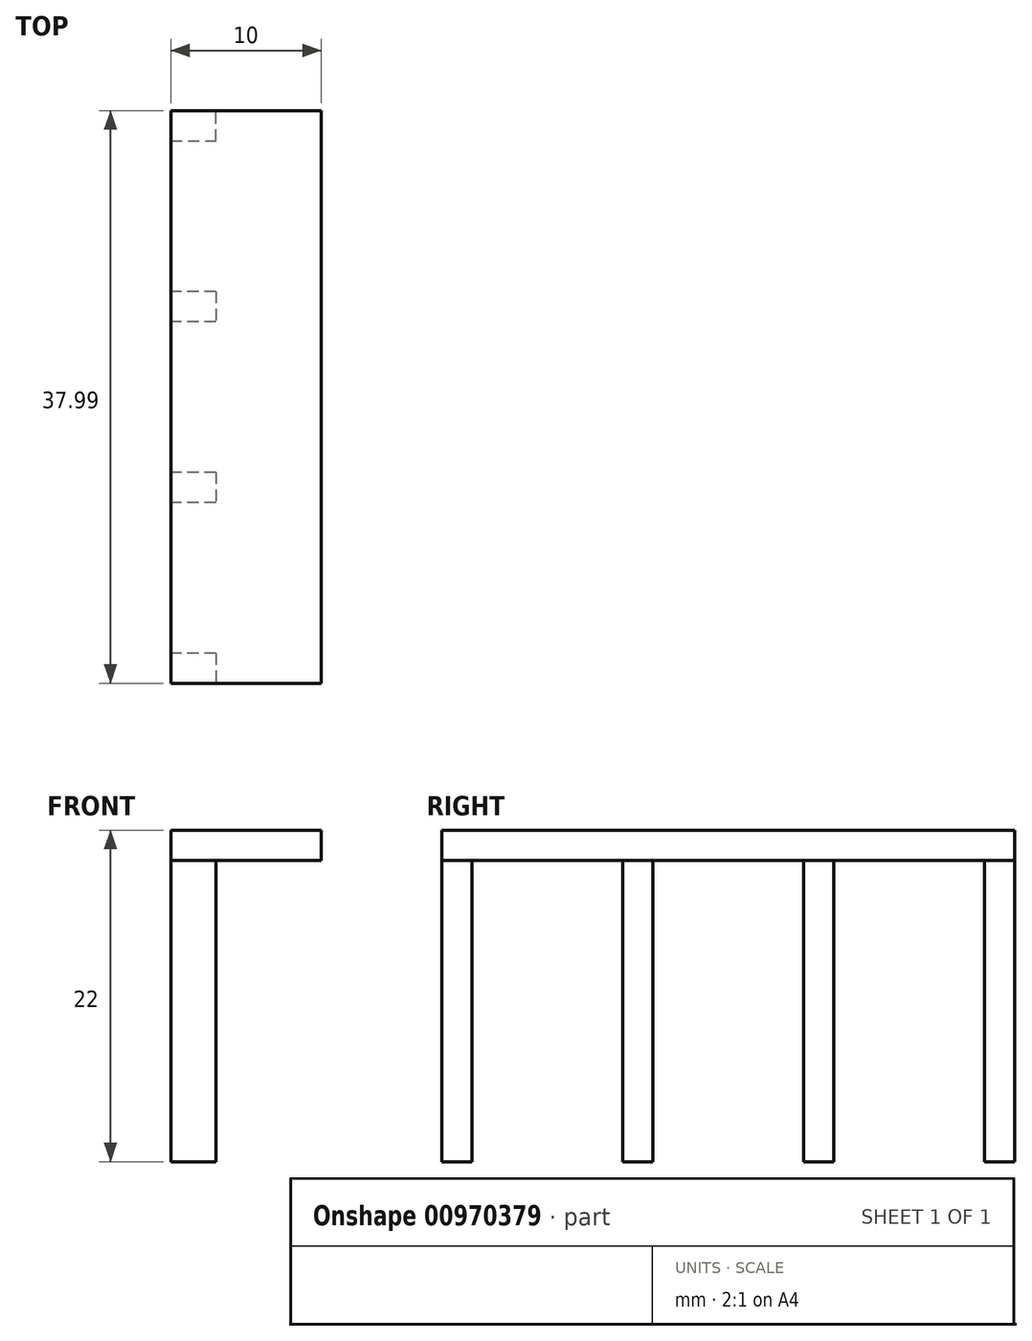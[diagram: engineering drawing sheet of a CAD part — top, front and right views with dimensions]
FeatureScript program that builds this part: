
annotation { "Feature Type Name" : "Feature", "Feature Type Description" : "" }
export const myFeature = defineFeature(function(context is Context, id is Id, definition is map)
    precondition{}
    {
        {
            var Q0;
            Q0=qCreatedBy(makeId("Top.planeOp"),FACE);
            var sketch = newSketch(context, id + "F0", { "sketchPlane" : qUnion([Q0])});
            skLineSegment(sketch, "E0.bottom", {"start": v(0, 0) * mm, "end": v(3, 0) * mm});
            skLineSegment(sketch, "E0.top", {"start": v(0, 2) * mm, "end": v(3, 2) * mm});
            skLineSegment(sketch, "E0.left", {"start": v(0, 0) * mm, "end": v(0, 2) * mm});
            skLineSegment(sketch, "E0.right", {"start": v(3, 0) * mm, "end": v(3, 2) * mm});
            skLineSegment(sketch, "E1", {"start": v(3, 0) * mm, "end": v(3, -10) * mm, "construction": true});
            skLineSegment(sketch, "E2", {"start": v(3, -10) * mm, "end": v(3, -22) * mm, "construction": true});
            skLineSegment(sketch, "E3", {"start": v(3, -22) * mm, "end": v(3, -34) * mm, "construction": true});
            skLineSegment(sketch, "E4", {"start": v(3, -34) * mm, "end": v(3, -46) * mm, "construction": true});
            skLineSegment(sketch, "E5", {"start": v(3, -46) * mm, "end": v(3, -58) * mm, "construction": true});
            skLineSegment(sketch, "E6.bottom", {"start": v(3, -10) * mm, "end": v(0, -10) * mm});
            skLineSegment(sketch, "E6.top", {"start": v(3, -12) * mm, "end": v(0, -12) * mm});
            skLineSegment(sketch, "E6.left", {"start": v(3, -10) * mm, "end": v(3, -12) * mm});
            skLineSegment(sketch, "E6.right", {"start": v(0, -10) * mm, "end": v(0, -12) * mm});
            skLineSegment(sketch, "E7.bottom", {"start": v(3, -22) * mm, "end": v(0, -22) * mm});
            skLineSegment(sketch, "E7.top", {"start": v(3, -24) * mm, "end": v(0, -24) * mm});
            skLineSegment(sketch, "E7.left", {"start": v(3, -22) * mm, "end": v(3, -24) * mm});
            skLineSegment(sketch, "E7.right", {"start": v(0, -22) * mm, "end": v(0, -24) * mm});
            skLineSegment(sketch, "E8.bottom", {"start": v(3, -34) * mm, "end": v(0, -34) * mm});
            skLineSegment(sketch, "E8.top", {"start": v(3, -36) * mm, "end": v(0, -36) * mm});
            skLineSegment(sketch, "E8.left", {"start": v(3, -34) * mm, "end": v(3, -36) * mm});
            skLineSegment(sketch, "E8.right", {"start": v(0, -34) * mm, "end": v(0, -36) * mm});
            skLineSegment(sketch, "E9.bottom", {"start": v(3, -46) * mm, "end": v(0, -46) * mm});
            skLineSegment(sketch, "E9.top", {"start": v(3, -48) * mm, "end": v(0, -48) * mm});
            skLineSegment(sketch, "E9.left", {"start": v(3, -46) * mm, "end": v(3, -48) * mm});
            skLineSegment(sketch, "E9.right", {"start": v(0, -46) * mm, "end": v(0, -48) * mm});
            skLineSegment(sketch, "E10.bottom", {"start": v(3, -58) * mm, "end": v(0, -58) * mm});
            skLineSegment(sketch, "E10.top", {"start": v(3, -60) * mm, "end": v(0, -60) * mm});
            skLineSegment(sketch, "E10.left", {"start": v(3, -58) * mm, "end": v(3, -60) * mm});
            skLineSegment(sketch, "E10.right", {"start": v(0, -58) * mm, "end": v(0, -60) * mm});
            skSolve(sketch);
        }
        {
            var Q0;
            Q0=qSketchRegion(id+"F0",true);
            extrude(context, id + "F1", {"entities" : qUnion([Q0]), "depth" : 20 * mm, "offsetDistance" : 25 * mm});
        }
        {
            var Q0;
            Q0=makeQuery(id+"F1.opExtrude","CAP_FACE",FACE,{"disambiguationData":[OSD([sQuery(id+"F0.wireOp",EDGE,"E0.bottom"),sQuery(id+"F0.wireOp",EDGE,"E0.top"),sQuery(id+"F0.wireOp",EDGE,"E0.left"),sQuery(id+"F0.wireOp",EDGE,"E0.right")])],"isStart":false});
            var sketch = newSketch(context, id + "F2", { "sketchPlane" : qUnion([Q0])});
            skLineSegment(sketch, "E11.bottom", {"start": v(0, 2) * mm, "end": v(10, 2) * mm});
            skLineSegment(sketch, "E11.top", {"start": v(0, -48) * mm, "end": v(10, -48) * mm});
            skLineSegment(sketch, "E11.left", {"start": v(0, 2) * mm, "end": v(0, -48) * mm});
            skLineSegment(sketch, "E11.right", {"start": v(10, 2) * mm, "end": v(10, -48) * mm});
            skSolve(sketch);
        }
        {
            var Q0;
            {var subQ4=makeQuery(id+"F1.opExtrude","CAP_EDGE",EDGE,{"disambiguationData":[OSD([sQuery(id+"F0.wireOp",EDGE,"E0.bottom")])],"isStart":false});Q0=makeQuery(id+"F2.imprint","IMPRINT",FACE,{"disambiguationData":[TD([[makeQuery(id+"F2.imprint","IMPRINT",EDGE,{"derivedFrom":subQ4}),1.0]])]});}
            var Q1;
            {var subQ3=sQuery(id+"F2.wireOp",EDGE,"E11.top");Q1=makeQuery(id+"F2.imprint","IMPRINT",FACE,{"disambiguationData":[TD([[makeQuery(id+"F2.imprint","IMPRINT",EDGE,{"derivedFrom":subQ3}),1.0]])]});}
            extrude(context, id + "F3", {"entities" : qUnion([Q0, Q1]), "depth" : 2 * mm, "offsetDistance" : 25 * mm});
        }
        {
            var Q0;
            Q0=makeQuery(id+"F1.opExtrude","CAP_FACE",FACE,{"disambiguationData":[OSD([sQuery(id+"F0.wireOp",EDGE,"E10.bottom"),sQuery(id+"F0.wireOp",EDGE,"E10.top"),sQuery(id+"F0.wireOp",EDGE,"E10.left"),sQuery(id+"F0.wireOp",EDGE,"E10.right")])],"isStart":false});
            var sketch = newSketch(context, id + "F4", { "sketchPlane" : qUnion([Q0])});
            skLineSegment(sketch, "E12.bottom", {"start": v(-1.97, -60) * mm, "end": v(5.06, -60) * mm});
            skLineSegment(sketch, "E12.top", {"start": v(-1.97, -56.22) * mm, "end": v(5.06, -56.22) * mm});
            skLineSegment(sketch, "E12.left", {"start": v(-1.97, -60) * mm, "end": v(-1.97, -56.22) * mm});
            skLineSegment(sketch, "E12.right", {"start": v(5.06, -60) * mm, "end": v(5.06, -56.22) * mm});
            skSolve(sketch);
        }
        {
            var Q0;
            Q0=qSketchRegion(id+"F4",true);
            extrude(context, id + "F5", {"entities" : qUnion([Q0]), "operationType" : NewBodyOperationType.REMOVE, "oppositeDirection" : true, "depth" : 25 * mm, "offsetDistance" : 25 * mm});
        }
        {
            var Q0;
            Q0=makeQuery(id+"F3.opExtrude","SWEPT_FACE",FACE,{"disambiguationData":[OSD([sQuery(id+"F2.wireOp",EDGE,"E11.left")])]});
            var sketch = newSketch(context, id + "F6", { "sketchPlane" : qUnion([Q0])});
            skLineSegment(sketch, "E13.bottom", {"start": v(35.99, 22) * mm, "end": v(48.01, 22) * mm});
            skLineSegment(sketch, "E13.top", {"start": v(35.99, 0) * mm, "end": v(48.01, 0) * mm});
            skLineSegment(sketch, "E13.left", {"start": v(35.99, 22) * mm, "end": v(35.99, 0) * mm});
            skLineSegment(sketch, "E13.right", {"start": v(48.01, 22) * mm, "end": v(48.01, 0) * mm});
            skSolve(sketch);
        }
        {
            var Q0;
            {var subQ1=sQuery(id+"F2.wireOp",EDGE,"E11.left");var subQ2=makeQuery(id+"F3.opExtrude","SWEPT_EDGE",EDGE,{"disambiguationData":[OSD([sQuery(id+"F2.wireOp",EDGE,"E11.top"),subQ1])]});Q0=makeQuery(id+"F6.imprint","IMPRINT",FACE,{"disambiguationData":[TD([[makeQuery(id+"F6.imprint","IMPRINT",EDGE,{"derivedFrom":subQ2}),-1.0]])]});}
            var Q1;
            {var subQ2=sQuery(id+"F6.wireOp",EDGE,"E13.top");Q1=makeQuery(id+"F6.imprint","IMPRINT",FACE,{"disambiguationData":[TD([[makeQuery(id+"F6.imprint","IMPRINT",EDGE,{"derivedFrom":subQ2}),1.0]])]});}
            extrude(context, id + "F7", {"entities" : qUnion([Q0, Q1]), "operationType" : NewBodyOperationType.REMOVE, "oppositeDirection" : true, "depth" : 25 * mm, "offsetDistance" : 25 * mm});
        }
    });
